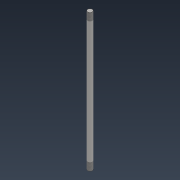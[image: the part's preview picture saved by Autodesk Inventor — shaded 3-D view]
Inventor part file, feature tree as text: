
AUTODESK INVENTOR PART (.ipt)
format: ipt  version: 2022 (Build 260153000, 153)  size: 82,432 bytes
history: native  units: mm
features: thread x2, extrude x1, sketch x1
ambient origin geometry x8: Origin, YZ Plane, XZ Plane, XY Plane, X Axis, Y Axis, Z Axis, Center Point
bodies: Solid1 (feature_tree)
feature tree (4):
  extrude  "Extrusion1"  Depth=300.0mm TaperAngle=0.0deg
  thread  "Thread1"  [1 undecoded]
  thread  "Thread2"  [1 undecoded]
  sketch  "Sketch1"  dims[d0=10.0mm d1=300.0mm d2=0.0mm d3=17.0mm d4=0.0mm d5=17.0mm d6=0.0mm]
note: 2 required parameter values undecoded (feature->parameter linkage not recoverable at this tier; creation-order binding heuristic only, values carry confidence <= 0.55)
